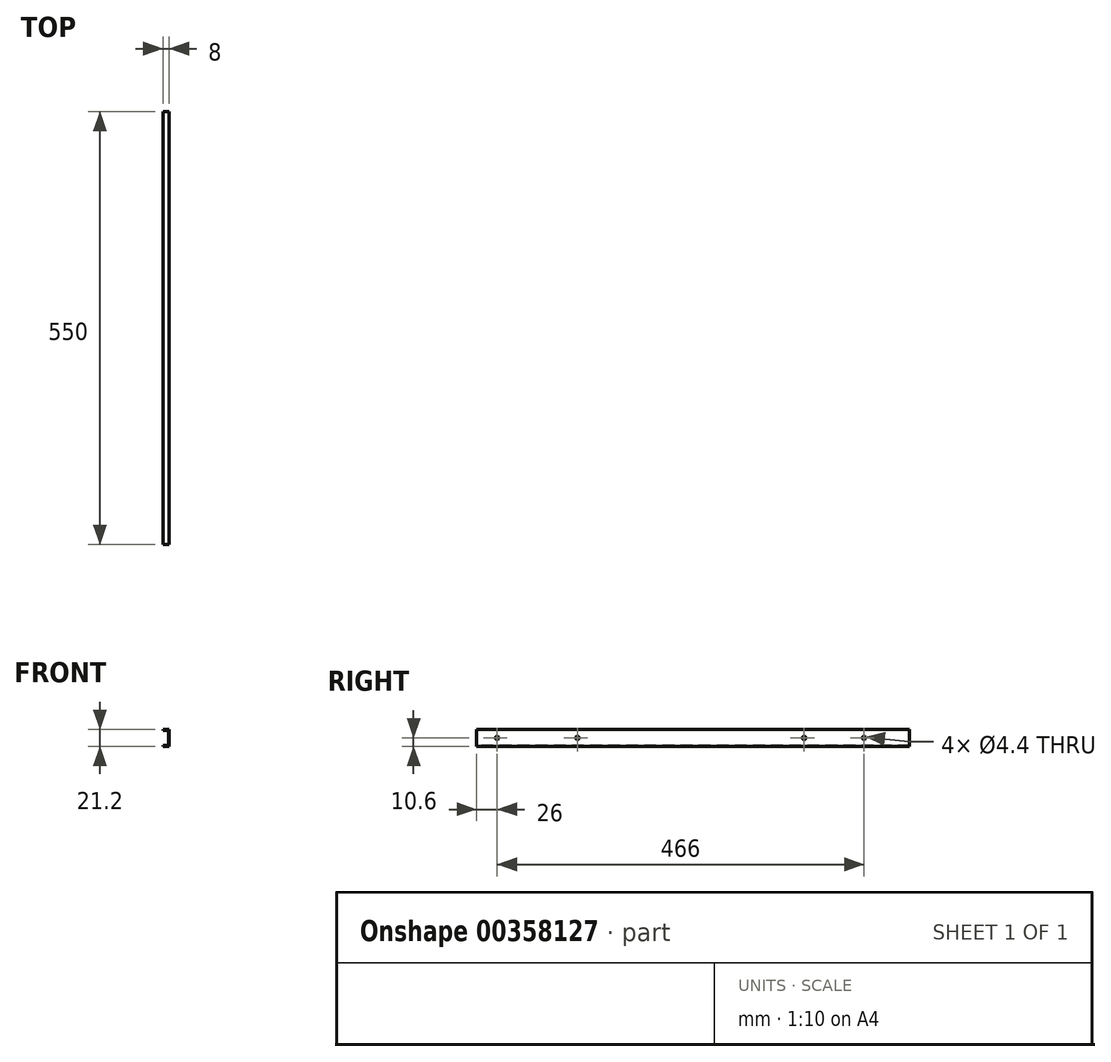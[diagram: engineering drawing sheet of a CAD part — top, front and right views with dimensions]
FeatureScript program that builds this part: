
annotation { "Feature Type Name" : "Feature", "Feature Type Description" : "" }
export const myFeature = defineFeature(function(context is Context, id is Id, definition is map)
    precondition{}
    {
        {
            var Q0;
            Q0=qCreatedBy(makeId("Front.planeOp"),FACE);
            var sketch = newSketch(context, id + "F0", { "sketchPlane" : qUnion([Q0])});
            skLineSegment(sketch, "E0.bottom", {"start": v(0, 0) * mm, "end": v(5, 0) * mm});
            skLineSegment(sketch, "E0.top", {"start": v(0, 42.87) * mm, "end": v(5, 42.87) * mm});
            skLineSegment(sketch, "E0.left", {"start": v(0, 0) * mm, "end": v(0, 42.87) * mm});
            skLineSegment(sketch, "E0.right", {"start": v(5, 12) * mm, "end": v(5, 13) * mm});
            skLineSegment(sketch, "E1.left", {"start": v(0, 0) * mm, "end": v(0, 12) * mm});
            skLineSegment(sketch, "E2.bottom", {"start": v(5, 12) * mm, "end": v(13, 12) * mm});
            skLineSegment(sketch, "E2.top", {"start": v(5, 33.2) * mm, "end": v(13, 33.2) * mm});
            skLineSegment(sketch, "E2.right", {"start": v(13, 12) * mm, "end": v(13, 33.2) * mm});
            skLineSegment(sketch, "E3.bottom", {"start": v(12, 32.2) * mm, "end": v(6, 32.2) * mm});
            skLineSegment(sketch, "E3.top", {"start": v(12, 13) * mm, "end": v(6, 13) * mm});
            skLineSegment(sketch, "E3.left", {"start": v(12, 32.2) * mm, "end": v(12, 13) * mm});
            skPoint(sketch, "E4.left.end.orphan", {"position": v(5, 13) * mm});
            skPoint(sketch, "E4.bottom.end.orphan", {"position": v(6, 12) * mm});
            skPoint(sketch, "E5.left.end.orphan", {"position": v(13, 32.2) * mm});
            skPoint(sketch, "E5.bottom.end.orphan", {"position": v(12, 33.2) * mm});
            skLineSegment(sketch, "E6", {"start": v(6, 13) * mm, "end": v(5, 13) * mm});
            skLineSegment(sketch, "E7", {"start": v(6, 32.2) * mm, "end": v(5, 32.2) * mm});
            skLineSegment(sketch, "E8.trimOffspring", {"start": v(5, 32.2) * mm, "end": v(5, 33.2) * mm});
            skSolve(sketch);
        }
        {
            var Q0;
            Q0=qSketchRegion(id+"F0",true);
            extrude(context, id + "F1", {"entities" : qUnion([Q0]), "depth" : -550 * mm});
        }
        {
            var Q0;
            Q0=makeQuery(id+"F1.opExtrude","SWEPT_FACE",FACE,{"disambiguationData":[OSD([sQuery(id+"F0.wireOp",EDGE,"E2.right")])]});
            var sketch = newSketch(context, id + "F2", { "sketchPlane" : qUnion([Q0])});
            skLineSegment(sketch, "E9", {"start": v(0, 22.6) * mm, "end": v(550, 22.6) * mm, "construction": true});
            skCircle(sketch, "E10", {"center": v(26, 22.6) * mm, "radius": 2.2 * mm});
            skCircle(sketch, "E11", {"center": v(128, 22.6) * mm, "radius": 2.2 * mm});
            skCircle(sketch, "E12", {"center": v(416, 22.6) * mm, "radius": 2.2 * mm});
            skCircle(sketch, "E13", {"center": v(492, 22.6) * mm, "radius": 2.2 * mm});
            skSolve(sketch);
        }
        {
            var Q0;
            Q0=qSketchRegion(id+"F2",true);
            extrude(context, id + "F3", {"entities" : qUnion([Q0]), "operationType" : NewBodyOperationType.REMOVE, "oppositeDirection" : true, "depth" : 1 * mm});
        }
    });
